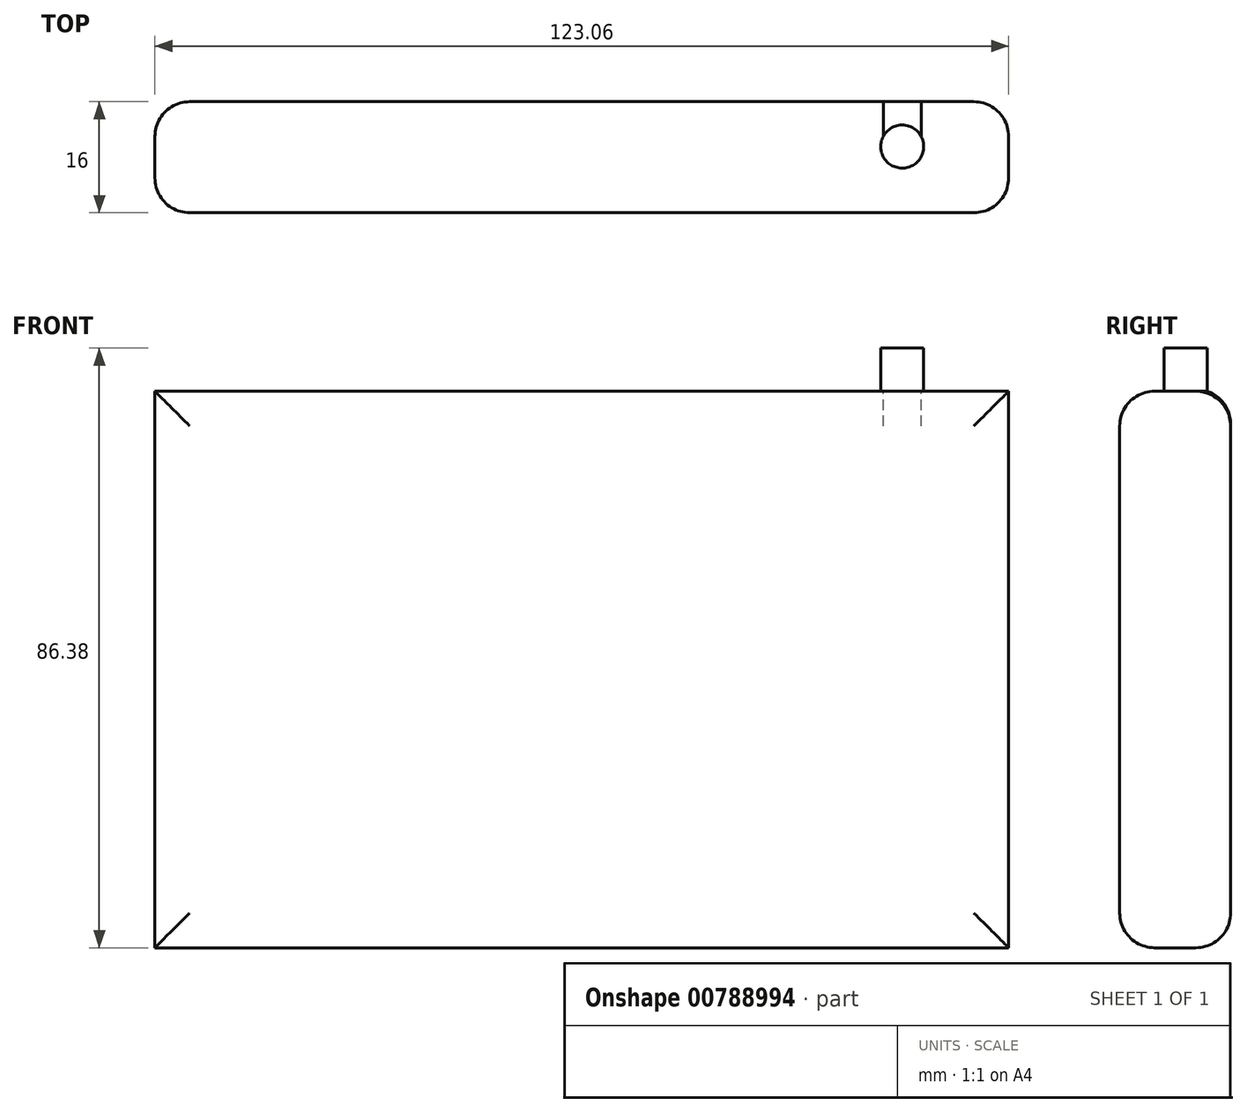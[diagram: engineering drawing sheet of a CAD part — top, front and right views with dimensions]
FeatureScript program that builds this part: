
annotation { "Feature Type Name" : "Feature", "Feature Type Description" : "" }
export const myFeature = defineFeature(function(context is Context, id is Id, definition is map)
    precondition{}
    {
        {
            var Q0;
            Q0=qCreatedBy(makeId("Front.planeOp"),FACE);
            var sketch = newSketch(context, id + "F0", { "sketchPlane" : qUnion([Q0])});
            skLineSegment(sketch, "E0.bottom", {"start": v(61.53, -40.08) * mm, "end": v(-61.52, -40.09) * mm});
            skLineSegment(sketch, "E0.top", {"start": v(61.52, 40.09) * mm, "end": v(-61.53, 40.08) * mm});
            skLineSegment(sketch, "E0.left", {"start": v(61.53, -40.08) * mm, "end": v(61.52, 40.09) * mm});
            skLineSegment(sketch, "E0.right", {"start": v(-61.52, -40.09) * mm, "end": v(-61.53, 40.08) * mm});
            skPoint(sketch, "E0.middle", {"position": v(0, 0) * mm});
            skSolve(sketch);
        }
        {
            var Q0;
            Q0 = qSketchRegion(id + "F0", true);
            extrude(context, id + "F1", {"entities" : qUnion([Q0]), "depth" : 16 * mm, "offsetDistance" : 25 * mm});
        }
        {
            var Q0;
            Q0=makeQuery(id+"F1.opExtrude","SWEPT_FACE",FACE,{"disambiguationData":[OSD([sQuery(id+"F0.wireOp",EDGE,"E0.top")])]});
            var sketch = newSketch(context, id + "F2", { "sketchPlane" : qUnion([Q0])});
            skCircle(sketch, "E1", {"center": v(46.18, -6.47) * mm, "radius": 3.1 * mm});
            skSolve(sketch);
        }
        {
            var Q0;
            Q0 = qSketchRegion(id + "F2", true);
            extrude(context, id + "F3", {"entities" : qUnion([Q0]), "operationType" : NewBodyOperationType.ADD, "depth" : 6.2 * mm, "offsetDistance" : 25 * mm});
        }
        {
            var Q0;
            Q0=makeQuery(id+"F1.opExtrude","CAP_EDGE",EDGE,{"disambiguationData":[OSD([sQuery(id+"F0.wireOp",EDGE,"E0.top")])],"isStart":true});
            var Q1;
            Q1=makeQuery(id+"F1.opExtrude","CAP_EDGE",EDGE,{"disambiguationData":[OSD([sQuery(id+"F0.wireOp",EDGE,"E0.right")])],"isStart":true});
            var Q2;
            Q2=makeQuery(id+"F1.opExtrude","CAP_EDGE",EDGE,{"disambiguationData":[OSD([sQuery(id+"F0.wireOp",EDGE,"E0.bottom")])],"isStart":true});
            var Q3;
            Q3=makeQuery(id+"F1.opExtrude","CAP_EDGE",EDGE,{"disambiguationData":[OSD([sQuery(id+"F0.wireOp",EDGE,"E0.left")])],"isStart":true});
            fillet(context, id + "F4", {"entities" : qUnion([Q0, Q1, Q2, Q3]), "radius" : 5 * mm, "tangentPropagation" : true, "allowEdgeOverflow" : false});
        }
        {
            var Q0;
            Q0=makeQuery(id+"F1.opExtrude","CAP_EDGE",EDGE,{"disambiguationData":[OSD([sQuery(id+"F0.wireOp",EDGE,"E0.top")])],"isStart":false});
            var Q1;
            Q1=makeQuery(id+"F1.opExtrude","CAP_EDGE",EDGE,{"disambiguationData":[OSD([sQuery(id+"F0.wireOp",EDGE,"E0.right")])],"isStart":false});
            var Q2;
            Q2=makeQuery(id+"F1.opExtrude","CAP_EDGE",EDGE,{"disambiguationData":[OSD([sQuery(id+"F0.wireOp",EDGE,"E0.bottom")])],"isStart":false});
            var Q3;
            Q3=makeQuery(id+"F1.opExtrude","CAP_EDGE",EDGE,{"disambiguationData":[OSD([sQuery(id+"F0.wireOp",EDGE,"E0.left")])],"isStart":false});
            fillet(context, id + "F5", {"entities" : qUnion([Q0, Q1, Q2, Q3]), "radius" : 5 * mm, "tangentPropagation" : true, "allowEdgeOverflow" : false});
        }
    });
